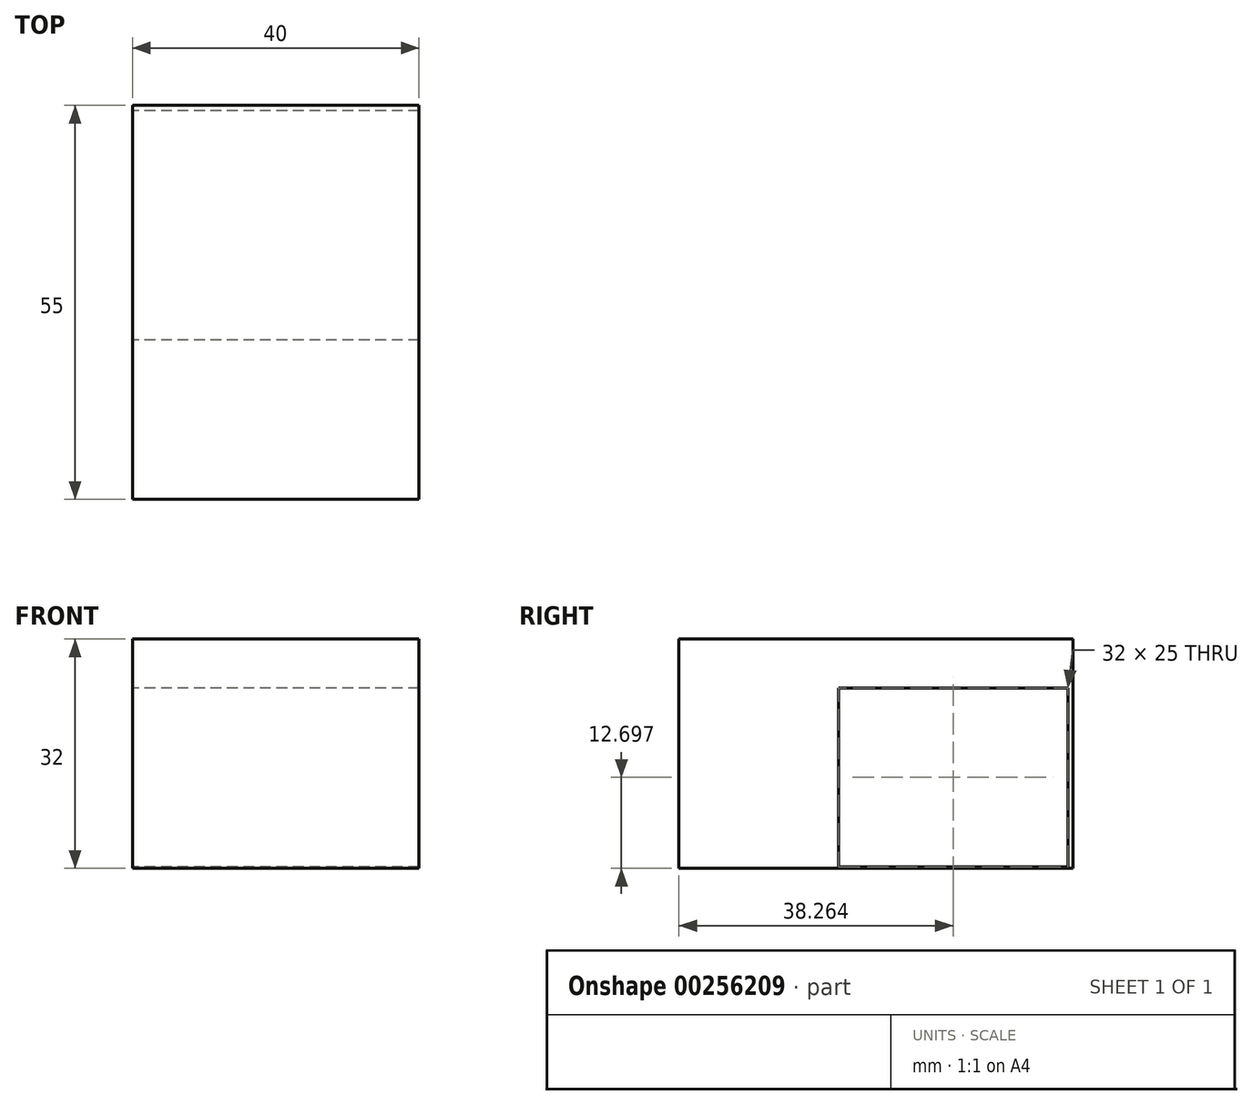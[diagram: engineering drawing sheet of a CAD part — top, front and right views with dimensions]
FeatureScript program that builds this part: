
annotation { "Feature Type Name" : "Feature", "Feature Type Description" : "" }
export const myFeature = defineFeature(function(context is Context, id is Id, definition is map)
    precondition{}
    {
        {
            var Q0;
            Q0=qCreatedBy(makeId("Right.planeOp"),FACE);
            var sketch = newSketch(context, id + "F0", { "sketchPlane" : qUnion([Q0])});
            skLineSegment(sketch, "E0.bottom", {"start": v(0, 0) * mm, "end": v(55, 0) * mm});
            skLineSegment(sketch, "E0.top", {"start": v(0, -32) * mm, "end": v(55, -32) * mm});
            skLineSegment(sketch, "E0.left", {"start": v(0, 0) * mm, "end": v(0, -32) * mm});
            skLineSegment(sketch, "E0.right", {"start": v(55, 0) * mm, "end": v(55, -32) * mm});
            skSolve(sketch);
        }
        {
            var Q0;
            Q0=makeQuery(id+"F0.imprint","IMPRINT",FACE,{"disambiguationData":[TD([[makeQuery(id+"F0.imprint","IMPRINT",EDGE,{"derivedFrom":sQuery(id+"F0.wireOp",EDGE,"E0.bottom")}),-1.0]])]});
            extrude(context, id + "F1", {"entities" : qUnion([Q0]), "depth" : 40 * mm});
        }
        {
            var Q0;
            Q0=qCreatedBy(makeId("Right.planeOp"),FACE);
            var sketch = newSketch(context, id + "F2", { "sketchPlane" : qUnion([Q0])});
            skLineSegment(sketch, "E1.bottom", {"start": v(54.26, -31.8) * mm, "end": v(22.26, -31.8) * mm});
            skLineSegment(sketch, "E1.top", {"start": v(54.26, -6.8) * mm, "end": v(22.26, -6.8) * mm});
            skLineSegment(sketch, "E1.left", {"start": v(54.26, -31.8) * mm, "end": v(54.26, -6.8) * mm});
            skLineSegment(sketch, "E1.right", {"start": v(22.26, -31.8) * mm, "end": v(22.26, -6.8) * mm});
            skSolve(sketch);
        }
        {
            var Q0;
            Q0 = qSketchRegion(id + "F2", true);
            extrude(context, id + "F3", {"entities" : qUnion([Q0]), "operationType" : NewBodyOperationType.REMOVE, "depth" : 40 * mm});
        }
    });
